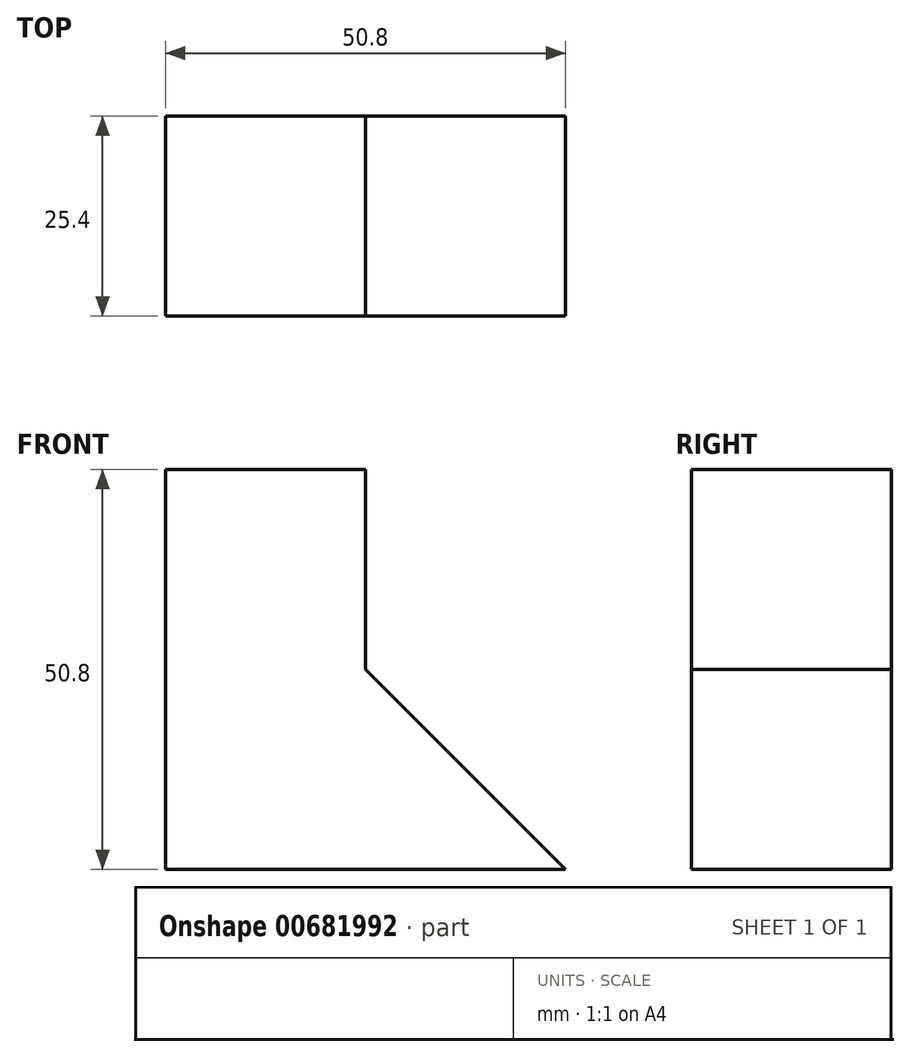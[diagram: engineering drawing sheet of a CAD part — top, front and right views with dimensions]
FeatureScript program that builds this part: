
annotation { "Feature Type Name" : "Feature", "Feature Type Description" : "" }
export const myFeature = defineFeature(function(context is Context, id is Id, definition is map)
    precondition{}
    {
        {
            var Q0;
            Q0=qCreatedBy(makeId("Front.planeOp"),FACE);
            var sketch = newSketch(context, id + "F0", { "sketchPlane" : qUnion([Q0])});
            skLineSegment(sketch, "E0", {"start": v(0, 0) * mm, "end": v(-50.8, 0) * mm});
            skLineSegment(sketch, "E1", {"start": v(-50.8, 0) * mm, "end": v(-50.8, 50.8) * mm});
            skLineSegment(sketch, "E2", {"start": v(-50.8, 50.8) * mm, "end": v(-25.4, 50.8) * mm});
            skLineSegment(sketch, "E3", {"start": v(-25.4, 50.8) * mm, "end": v(-25.4, 25.4) * mm});
            skLineSegment(sketch, "E4", {"start": v(-25.4, 25.4) * mm, "end": v(0, 0) * mm});
            skSolve(sketch);
        }
        {
            var Q0;
            Q0=makeQuery(id+"F0.imprint","IMPRINT",FACE,{"disambiguationData":[TD([[makeQuery(id+"F0.imprint","IMPRINT",EDGE,{"derivedFrom":sQuery(id+"F0.wireOp",EDGE,"E0")}),-1.0]])]});
            extrude(context, id + "F1", {"entities" : qUnion([Q0]), "depth" : 25.4 * mm, "offsetDistance" : 25.4 * mm});
        }
    });
